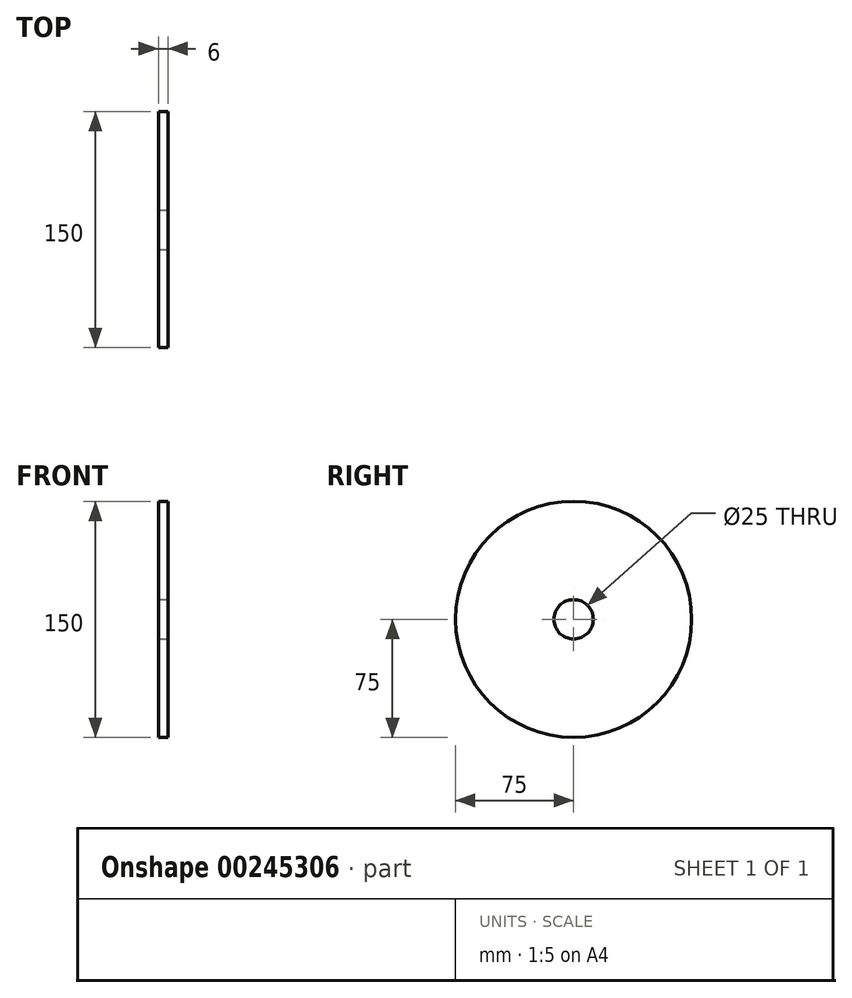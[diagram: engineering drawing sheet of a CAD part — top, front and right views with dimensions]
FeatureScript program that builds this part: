
annotation { "Feature Type Name" : "Feature", "Feature Type Description" : "" }
export const myFeature = defineFeature(function(context is Context, id is Id, definition is map)
    precondition{}
    {
        {
            var Q0;
            Q0=qCreatedBy(makeId("Right.planeOp"),FACE);
            var sketch = newSketch(context, id + "F0", { "sketchPlane" : qUnion([Q0])});
            skCircle(sketch, "E0", {"center": v(0, 0) * mm, "radius": 75 * mm});
            skSolve(sketch);
        }
        {
            var Q0;
            Q0 = qSketchRegion(id + "F0", true);
            extrude(context, id + "F1", {"entities" : qUnion([Q0]), "depth" : 6 * mm, "offsetDistance" : 25 * mm});
        }
        {
            var Q0;
            Q0=makeQuery(id+"F1.opExtrude","CAP_FACE",FACE,{"disambiguationData":[OSD([sQuery(id+"F0.wireOp",EDGE,"E0")])],"isStart":false});
            var sketch = newSketch(context, id + "F2", { "sketchPlane" : qUnion([Q0])});
            skCircle(sketch, "E1", {"center": v(0, 0) * mm, "radius": 12.5 * mm});
            skSolve(sketch);
        }
        {
            var Q0;
            Q0 = qSketchRegion(id + "F2", true);
            extrude(context, id + "F3", {"entities" : qUnion([Q0]), "operationType" : NewBodyOperationType.REMOVE, "endBound" : BoundingType.THROUGH_ALL, "oppositeDirection" : true, "depth" : 25 * mm, "offsetDistance" : 25 * mm});
        }
    });
